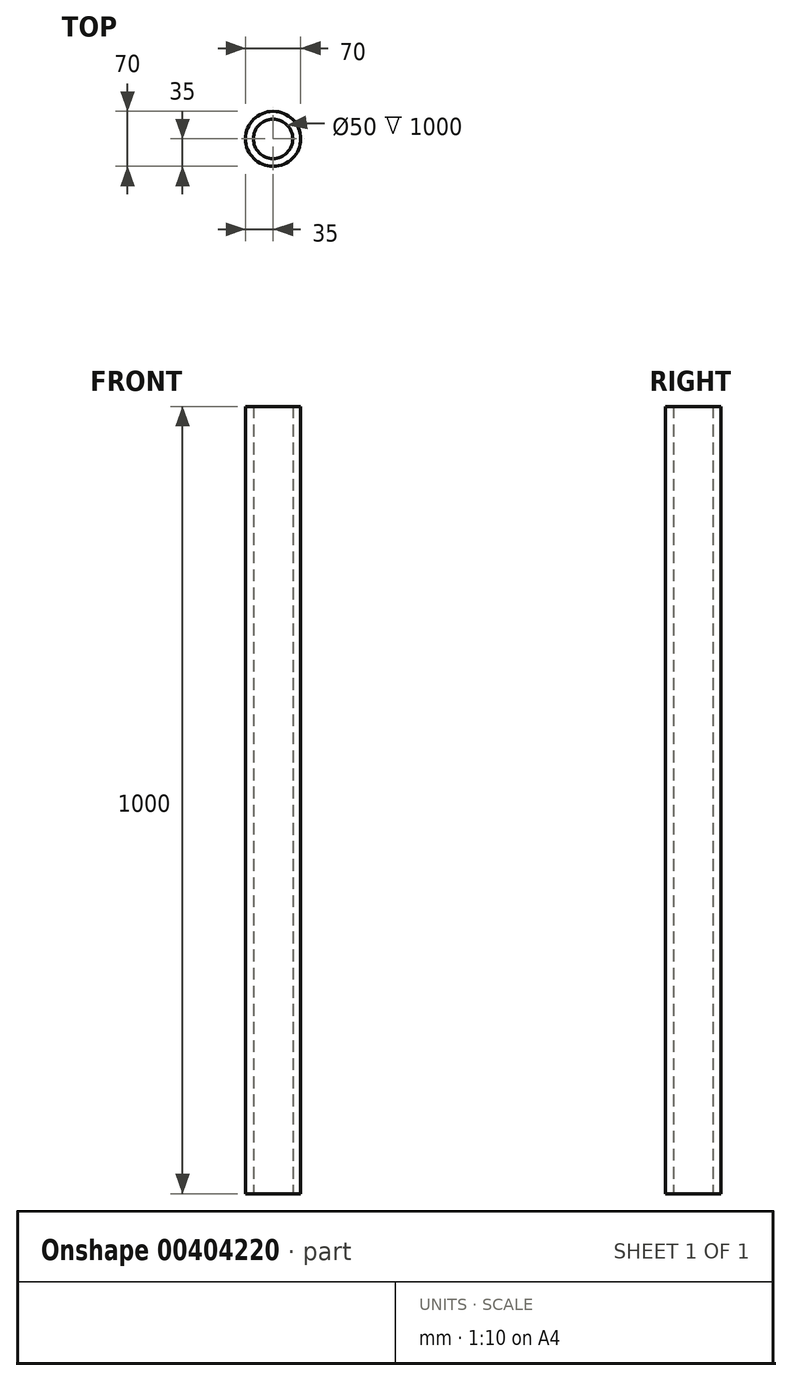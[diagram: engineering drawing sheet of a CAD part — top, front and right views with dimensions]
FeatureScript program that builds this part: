
annotation { "Feature Type Name" : "Feature", "Feature Type Description" : "" }
export const myFeature = defineFeature(function(context is Context, id is Id, definition is map)
    precondition{}
    {
        {
            var Q0;
            Q0=qCreatedBy(makeId("Top.planeOp"),FACE);
            var sketch = newSketch(context, id + "F0", { "sketchPlane" : qUnion([Q0])});
            skCircle(sketch, "E0", {"center": v(0, 0) * mm, "radius": 25 * mm});
            skCircle(sketch, "E1", {"center": v(0, 0) * mm, "radius": 35 * mm});
            skSolve(sketch);
        }
        {
            var Q0;
            Q0=makeQuery(id+"F0.imprint","IMPRINT",FACE,{"disambiguationData":[TD([[makeQuery(id+"F0.imprint","IMPRINT",EDGE,{"derivedFrom":sQuery(id+"F0.wireOp",EDGE,"E0")}),-1.0]])]});
            extrude(context, id + "F1", {"entities" : qUnion([Q0]), "depth" : 1000 * mm});
        }
    });
